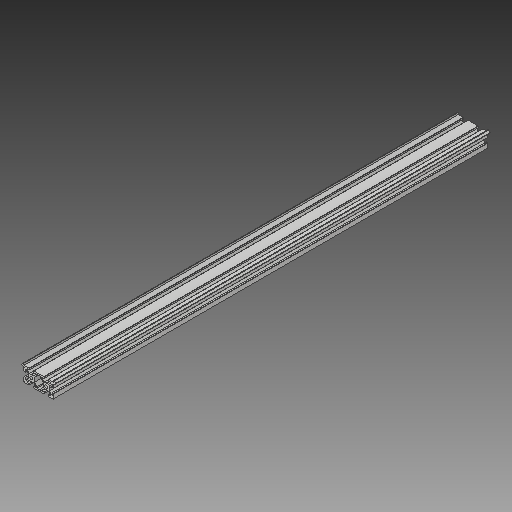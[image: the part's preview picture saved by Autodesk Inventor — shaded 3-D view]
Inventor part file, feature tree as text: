
AUTODESK INVENTOR PART (.ipt)
format: ipt  version: 2018 (Build 220112000, 112)  size: 233,984 bytes
history: native  units: mm
features: other x2, extrude x1, sketch x1, reference x1
ambient origin geometry x8: Origin, YZ Plane, XZ Plane, XY Plane, X Axis, Y Axis, Z Axis, Center Point
bodies: Solid1 (feature_tree)
feature tree (5):
  extrude  "Extrusion1"  [1 undecoded]
  sketch  "Sketch1"  dims[d0=585.0mm d1=0.0mm]
  reference  "Reference1"
  other  "Assembly3"
  other  "Makerslide 600mm:1"
note: 1 required parameter value undecoded (feature->parameter linkage not recoverable at this tier; creation-order binding heuristic only, values carry confidence <= 0.55)
